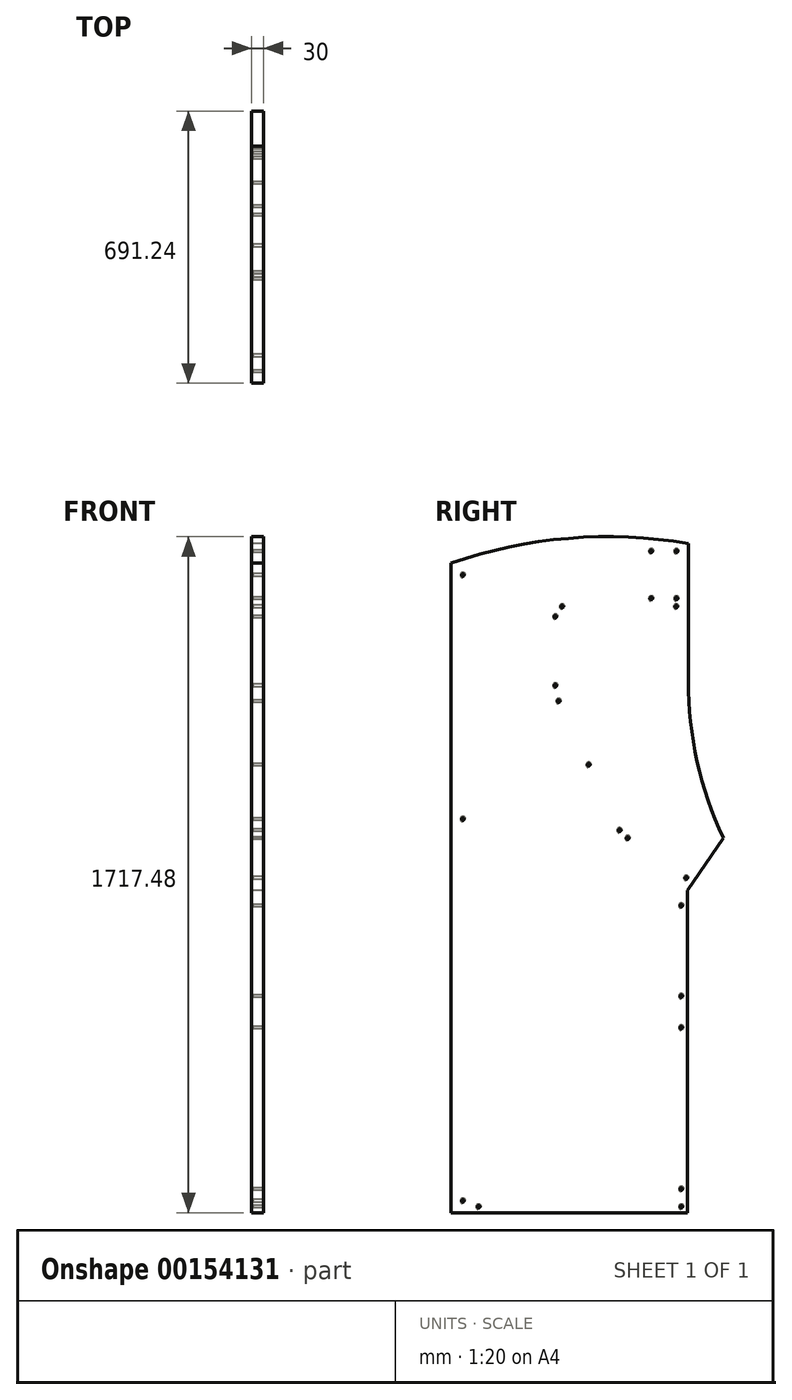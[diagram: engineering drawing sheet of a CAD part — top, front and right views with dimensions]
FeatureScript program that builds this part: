
annotation { "Feature Type Name" : "Feature", "Feature Type Description" : "" }
export const myFeature = defineFeature(function(context is Context, id is Id, definition is map)
    precondition{}
    {
        {
            var Q0;
            Q0=qCreatedBy(makeId("Right.planeOp"),FACE);
            var sketch = newSketch(context, id + "F0", { "sketchPlane" : qUnion([Q0])});
            skLineSegment(sketch, "E0", {"start": v(-279, -818.5) * mm, "end": v(-279, 831.5) * mm});
            skLineSegment(sketch, "E1", {"start": v(321, 0) * mm, "end": v(321, -818.5) * mm});
            skLineSegment(sketch, "E2", {"start": v(321, -818.5) * mm, "end": v(-279, -818.5) * mm});
            skArc(sketch, "E3", {"start": v(323.62, 881.5) * mm, "mid": v(19.13, 894.86) * mm, "end": v(-279, 831.5) * mm});
            skLineSegment(sketch, "E4", {"start": v(323.62, 881.5) * mm, "end": v(323.62, 532) * mm});
            skLineSegment(sketch, "E5", {"start": v(321, 0) * mm, "end": v(412.24, 134.02) * mm});
            skArc(sketch, "E6", {"start": v(323.62, 532) * mm, "mid": v(346.05, 328.14) * mm, "end": v(412.24, 134.02) * mm});
            skPoint(sketch, "E7", {"position": v(-249, -788.5) * mm});
            skPoint(sketch, "E8", {"position": v(306, -803.5) * mm});
            skPoint(sketch, "E9", {"position": v(306, -38.5) * mm});
            skPoint(sketch, "E10", {"position": v(293.62, 862) * mm});
            skPoint(sketch, "E11", {"position": v(293.62, 742) * mm});
            skPoint(sketch, "E12", {"position": v(-249, 801.5) * mm});
            skPoint(sketch, "E13", {"position": v(-249, 181.5) * mm});
            skPoint(sketch, "E14", {"position": v(318.52, 31.89) * mm});
            skPoint(sketch, "E15", {"position": v(229.62, 862) * mm});
            skPoint(sketch, "E16", {"position": v(229.62, 742) * mm});
            skPoint(sketch, "E17", {"position": v(306, -758.5) * mm});
            skPoint(sketch, "E18", {"position": v(306, -348.5) * mm});
            skPoint(sketch, "E19", {"position": v(-209, -803.5) * mm});
            skPoint(sketch, "E20", {"position": v(169.73, 133.19) * mm});
            skLineSegment(sketch, "E21", {"start": v(169.73, 133.19) * mm, "end": v(318.52, 31.89) * mm});
            skPoint(sketch, "E22", {"position": v(306, -268.5) * mm});
            skPoint(sketch, "E23", {"position": v(149.01, 152.93) * mm});
            skPoint(sketch, "E24", {"position": v(70.59, 319.38) * mm});
            skPoint(sketch, "E25", {"position": v(-5.7, 481.3) * mm});
            skLineSegment(sketch, "E26", {"start": v(-5.7, 481.3) * mm, "end": v(70.59, 319.38) * mm});
            skLineSegment(sketch, "E27", {"start": v(70.59, 319.38) * mm, "end": v(149.01, 152.93) * mm});
            skPoint(sketch, "E28", {"position": v(-14, 520.77) * mm});
            skPoint(sketch, "E29", {"position": v(-14, 695.77) * mm});
            skPoint(sketch, "E30", {"position": v(3.03, 721.42) * mm});
            skPoint(sketch, "E31", {"position": v(293.03, 721.42) * mm});
            skLineSegment(sketch, "E32", {"start": v(3.03, 721.42) * mm, "end": v(293.03, 721.42) * mm});
            skSolve(sketch);
        }
        {
            var Q0;
            Q0=makeQuery(id+"F0.imprint","IMPRINT",FACE,{"disambiguationData":[TD([[makeQuery(id+"F0.imprint","IMPRINT",EDGE,{"derivedFrom":sQuery(id+"F0.wireOp",EDGE,"E0")}),-1.0]])]});
            extrude(context, id + "F1", {"entities" : qUnion([Q0]), "depth" : 30 * mm});
        }
        {
            var Q0;
            Q0=sQuery(id+"F0.wireOp",VERTEX,"b9837053-11db-4487-8885-cea22af114a3");
            var Q1;
            Q1=sQuery(id+"F0.wireOp",VERTEX,"E11");
            var Q2;
            Q2=sQuery(id+"F0.wireOp",VERTEX,"E10");
            var Q3;
            Q3=sQuery(id+"F0.wireOp",VERTEX,"E15");
            var Q4;
            Q4=sQuery(id+"F0.wireOp",VERTEX,"E16");
            var Q5;
            Q5=sQuery(id+"F0.wireOp",VERTEX,"E12");
            var Q6;
            Q6=sQuery(id+"F0.wireOp",VERTEX,"E13");
            var Q7;
            Q7=sQuery(id+"F0.wireOp",VERTEX,"E9");
            var Q8;
            Q8=sQuery(id+"F0.wireOp",VERTEX,"E18");
            var Q9;
            Q9=sQuery(id+"F0.wireOp",VERTEX,"E17");
            var Q10;
            Q10=sQuery(id+"F0.wireOp",VERTEX,"E8");
            var Q11;
            Q11=sQuery(id+"F0.wireOp",VERTEX,"E19");
            var Q12;
            Q12=sQuery(id+"F0.wireOp",VERTEX,"E7");
            var Q13;
            Q13=sQuery(id+"F0.wireOp",VERTEX,"E22");
            var Q14;
            Q14=sQuery(id+"F0.wireOp",VERTEX,"E14");
            var Q15;
            Q15=sQuery(id+"F0.wireOp",VERTEX,"E20");
            var Q16;
            Q16=sQuery(id+"F0.wireOp",VERTEX,"E23");
            var Q17;
            Q17=sQuery(id+"F0.wireOp",VERTEX,"E24");
            var Q18;
            Q18=sQuery(id+"F0.wireOp",VERTEX,"E25");
            var Q19;
            Q19=sQuery(id+"F0.wireOp",VERTEX,"E28");
            var Q20;
            Q20=sQuery(id+"F0.wireOp",VERTEX,"E29");
            var Q21;
            Q21=sQuery(id+"F0.wireOp",VERTEX,"E31");
            var Q22;
            Q22=sQuery(id+"F0.wireOp",VERTEX,"E30");
            var Q23;
            Q23=makeQuery(id+"F1.opExtrude","SWEPT_BODY",BODY,{"disambiguationData":[OSD([sQuery(id+"F0.wireOp",EDGE,"E0"),sQuery(id+"F0.wireOp",EDGE,"E1"),sQuery(id+"F0.wireOp",EDGE,"E2"),sQuery(id+"F0.wireOp",EDGE,"E3"),sQuery(id+"F0.wireOp",EDGE,"E4"),sQuery(id+"F0.wireOp",EDGE,"E5"),sQuery(id+"F0.wireOp",EDGE,"E6")])]});
            hole(context, id + "F2", {"style" : HoleStyle.C_SINK, "endStyle" : HoleEndStyle.THROUGH, "oppositeDirection" : true, "standardTappedOrClearance" : lookupTablePath({ "standard" : "ISO", "fit" : "Normal", "size" : "M6", "type" : "Clearance" }), "standardBlindInLast" : lookupTablePath({ "fit" : "Standard", "standard" : "ISO", "size" : "M6", "type" : "Clearance" }), "holeDiameter" : 6.6 * mm, "cSinkDiameter" : 13.44 * mm, "cSinkAngle" : 90 * degree, "locations" : qUnion([Q0, Q1, Q2, Q3, Q4, Q5, Q6, Q7, Q8, Q9, Q10, Q11, Q12, Q13, Q14, Q15, Q16, Q17, Q18, Q19, Q20, Q21, Q22]), "scope" : qUnion([Q23]), "isTappedThrough" : true});
        }
    });
